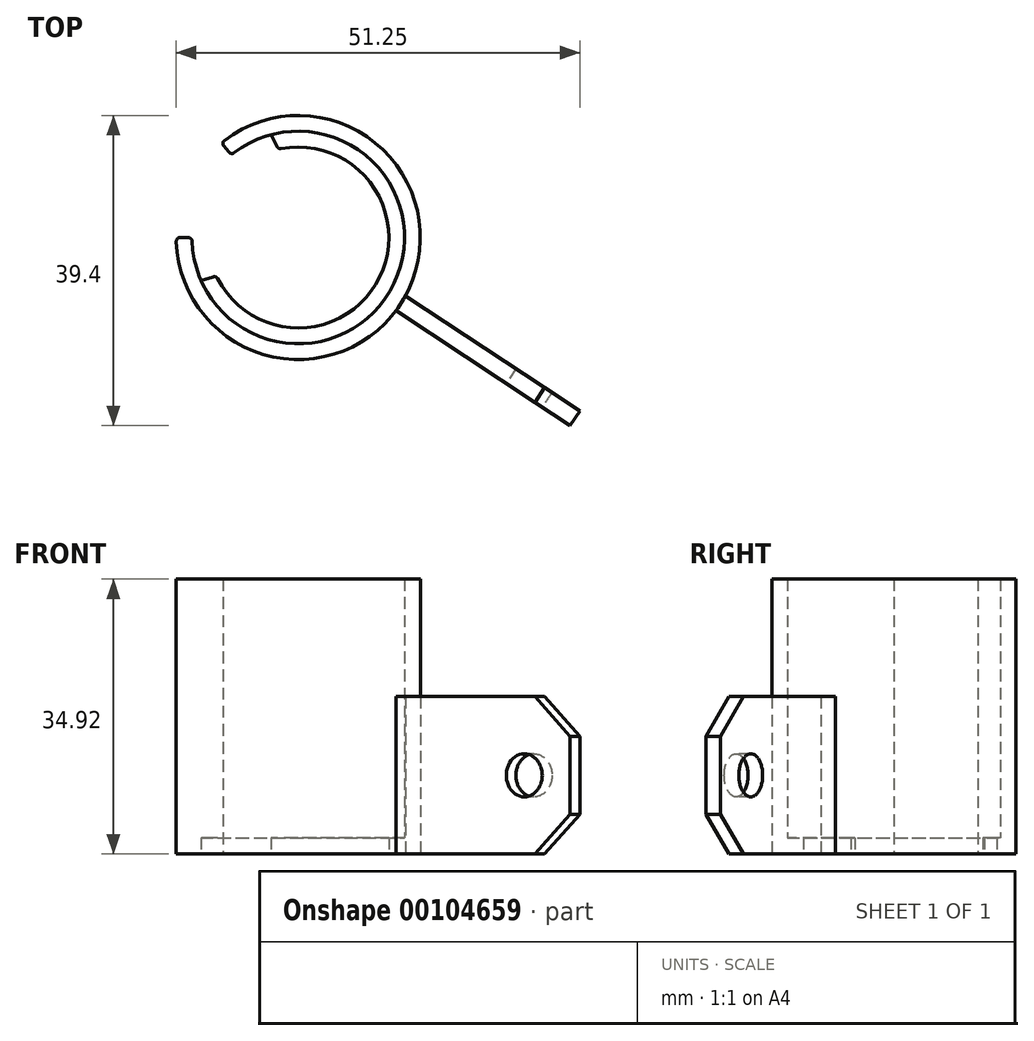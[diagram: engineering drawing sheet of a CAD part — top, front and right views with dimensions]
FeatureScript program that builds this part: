
annotation { "Feature Type Name" : "Feature", "Feature Type Description" : "" }
export const myFeature = defineFeature(function(context is Context, id is Id, definition is map)
    precondition{}
    {
        {
            var Q0;
            Q0=qCreatedBy(makeId("Top.planeOp"),FACE);
            var sketch = newSketch(context, id + "F0", { "sketchPlane" : qUnion([Q0])});
            skArc(sketch, "E0", {"start": v(-13.5, -0.47) * mm, "mid": v(12.19, -5.8) * mm, "end": v(-8.14, 10.77) * mm});
            skArc(sketch, "E1.0", {"start": v(-15.5, -0.5) * mm, "mid": v(14, -6.66) * mm, "end": v(-9.38, 12.34) * mm});
            skLineSegment(sketch, "E2", {"start": v(-15, 0) * mm, "end": v(-13.98, 0) * mm});
            skPoint(sketch, "E3.visualSharp", {"position": v(-13.5, 0) * mm});
            skArc(sketch, "E3.filletArc", {"start": v(-13.5, -0.47) * mm, "mid": v(-13.64, -0.14) * mm, "end": v(-13.98, 0) * mm});
            skPoint(sketch, "E4.visualSharp", {"position": v(-15.5, 0) * mm});
            skArc(sketch, "E4.filletArc", {"start": v(-15, 0) * mm, "mid": v(-15.35, -0.15) * mm, "end": v(-15.5, -0.5) * mm});
            skLineSegment(sketch, "E5", {"start": v(-9.46, 11.65) * mm, "end": v(-8.81, 10.85) * mm});
            skPoint(sketch, "E6.visualSharp", {"position": v(-9.77, 12.03) * mm});
            skArc(sketch, "E6.filletArc", {"start": v(-9.38, 12.34) * mm, "mid": v(-9.57, 12.01) * mm, "end": v(-9.46, 11.65) * mm});
            skPoint(sketch, "E7.visualSharp", {"position": v(-8.51, 10.48) * mm});
            skArc(sketch, "E7.filletArc", {"start": v(-8.81, 10.85) * mm, "mid": v(-8.5, 10.67) * mm, "end": v(-8.14, 10.77) * mm});
            skArc(sketch, "E8.0", {"start": v(-10.24, -5.24) * mm, "mid": v(10.34, -5.04) * mm, "end": v(-2.17, 11.3) * mm});
            skLineSegment(sketch, "E9", {"start": v(-3.43, 13.06) * mm, "end": v(-2.7, 11.56) * mm});
            skPoint(sketch, "E10", {"position": v(-10.82, -3.9) * mm});
            skPoint(sketch, "E11", {"position": v(-10.54, -4.6) * mm});
            skLineSegment(sketch, "E12", {"start": v(-10.81, -5) * mm, "end": v(-12.35, -5.46) * mm});
            skPoint(sketch, "E13.orphan", {"position": v(-11.5, -0.4) * mm});
            skPoint(sketch, "E14.orphan", {"position": v(-6.93, 9.17) * mm});
            skPoint(sketch, "E15.visualSharp", {"position": v(-2.53, 11.22) * mm});
            skArc(sketch, "E15.filletArc", {"start": v(-2.7, 11.56) * mm, "mid": v(-2.48, 11.34) * mm, "end": v(-2.17, 11.3) * mm});
            skPoint(sketch, "E16.visualSharp", {"position": v(-10.41, -4.88) * mm});
            skArc(sketch, "E16.filletArc", {"start": v(-10.24, -5.24) * mm, "mid": v(-10.48, -5.02) * mm, "end": v(-10.81, -5) * mm});
            skLineSegment(sketch, "E17", {"start": v(12.42, -9.28) * mm, "end": v(34.53, -23.9) * mm});
            skLineSegment(sketch, "E18", {"start": v(35.21, -23.76) * mm, "end": v(35.22, -23.74) * mm});
            skPoint(sketch, "E19.visualSharp", {"position": v(34.94, -24.17) * mm});
            skPoint(sketch, "E20.visualSharp", {"position": v(35.5, -23.33) * mm});
            skLineSegment(sketch, "E21.0", {"start": v(13.65, -7.41) * mm, "end": v(35.76, -22.03) * mm});
            skLineSegment(sketch, "E22", {"start": v(13.65, -7.41) * mm, "end": v(13.62, -7.4) * mm});
            skLineSegment(sketch, "E23", {"start": v(34.53, -23.9) * mm, "end": v(35.76, -22.03) * mm});
            skSolve(sketch);
        }
        {
            var Q0;
            Q0=makeQuery(id+"F0.imprint","IMPRINT",FACE,{"disambiguationData":[TD([[makeQuery(id+"F0.imprint","IMPRINT",EDGE,{"derivedFrom":sQuery(id+"F0.wireOp",EDGE,"E0")}),-1.0]])]});
            extrude(context, id + "F1", {"entities" : qUnion([Q0]), "depth" : 34.92 * mm});
        }
        {
            var Q0;
            Q0=makeQuery(id+"F0.imprint","IMPRINT",FACE,{"disambiguationData":[TD([[makeQuery(id+"F0.imprint","IMPRINT",EDGE,{"derivedFrom":sQuery(id+"F0.wireOp",EDGE,"E8.0")}),-1.0]])]});
            extrude(context, id + "F2", {"entities" : qUnion([Q0]), "operationType" : NewBodyOperationType.ADD, "depth" : 2.06 * mm});
        }
        {
            var Q0;
            {var subQ0=sQuery(id+"F0.wireOp",EDGE,"E17");Q0=makeQuery(id+"F0.imprint","IMPRINT",FACE,{"disambiguationData":[TD([[makeQuery(id+"F0.imprint","IMPRINT",EDGE,{"derivedFrom":subQ0}),1.0]])]});}
            extrude(context, id + "F3", {"entities" : qUnion([Q0]), "operationType" : NewBodyOperationType.ADD, "depth" : 19.99 * mm});
        }
        {
            var Q0;
            Q0=makeQuery(id+"F3.opExtrude","SWEPT_FACE",FACE,{"disambiguationData":[OSD([sQuery(id+"F0.wireOp",EDGE,"E17")])]});
            var sketch = newSketch(context, id + "F4", { "sketchPlane" : qUnion([Q0])});
            skLineSegment(sketch, "E24", {"start": v(36.63, 19.99) * mm, "end": v(41.99, 14.93) * mm});
            skPoint(sketch, "E25", {"position": v(41.99, 19.99) * mm});
            skPoint(sketch, "E26", {"position": v(41.99, 5.05) * mm});
            skLineSegment(sketch, "E27", {"start": v(36.63, 0) * mm, "end": v(41.99, 5.05) * mm});
            skLineSegment(sketch, "E28", {"start": v(36.63, 19.99) * mm, "end": v(41.99, 19.99) * mm});
            skLineSegment(sketch, "E29", {"start": v(36.63, 0) * mm, "end": v(41.99, 0) * mm});
            skLineSegment(sketch, "E30", {"start": v(41.99, 0) * mm, "end": v(41.99, 5.05) * mm});
            skSolve(sketch);
        }
        {
            var Q0;
            Q0 = qSketchRegion(id + "F4", true);
            var Q1;
            {var subQ0=sQuery(id+"F4.wireOp",EDGE,"E24");Q1=makeQuery(id+"F4.imprint","IMPRINT",FACE,{"disambiguationData":[TD([[makeQuery(id+"F4.imprint","IMPRINT",EDGE,{"derivedFrom":subQ0}),1.0]])]});}
            extrude(context, id + "F5", {"entities" : qUnion([Q0, Q1]), "operationType" : NewBodyOperationType.REMOVE, "oppositeDirection" : true, "depth" : 25.4 * mm});
        }
        {
            var Q0;
            Q0=makeQuery(id+"F3.opExtrude","SWEPT_FACE",FACE,{"disambiguationData":[OSD([sQuery(id+"F0.wireOp",EDGE,"E17")])]});
            var sketch = newSketch(context, id + "F6", { "sketchPlane" : qUnion([Q0])});
            skPoint(sketch, "E31", {"position": v(15.47, 10) * mm});
            skPoint(sketch, "E32", {"position": v(35, 10) * mm});
            skPoint(sketch, "E33.orphan", {"position": v(15.47, 19.99) * mm});
            skCircle(sketch, "E34", {"center": v(35, 10) * mm, "radius": 2.74 * mm});
            skSolve(sketch);
        }
        {
            var Q0;
            Q0=makeQuery(id+"F6.imprint","IMPRINT",FACE,{"disambiguationData":[TD([[makeQuery(id+"F6.imprint","IMPRINT",EDGE,{"derivedFrom":sQuery(id+"F6.wireOp",EDGE,"E34")}),1.0]])]});
            extrude(context, id + "F7", {"entities" : qUnion([Q0]), "operationType" : NewBodyOperationType.REMOVE, "oppositeDirection" : true, "offsetDistance" : 25.4 * mm, "depth" : 6.35 * mm});
        }
    });
